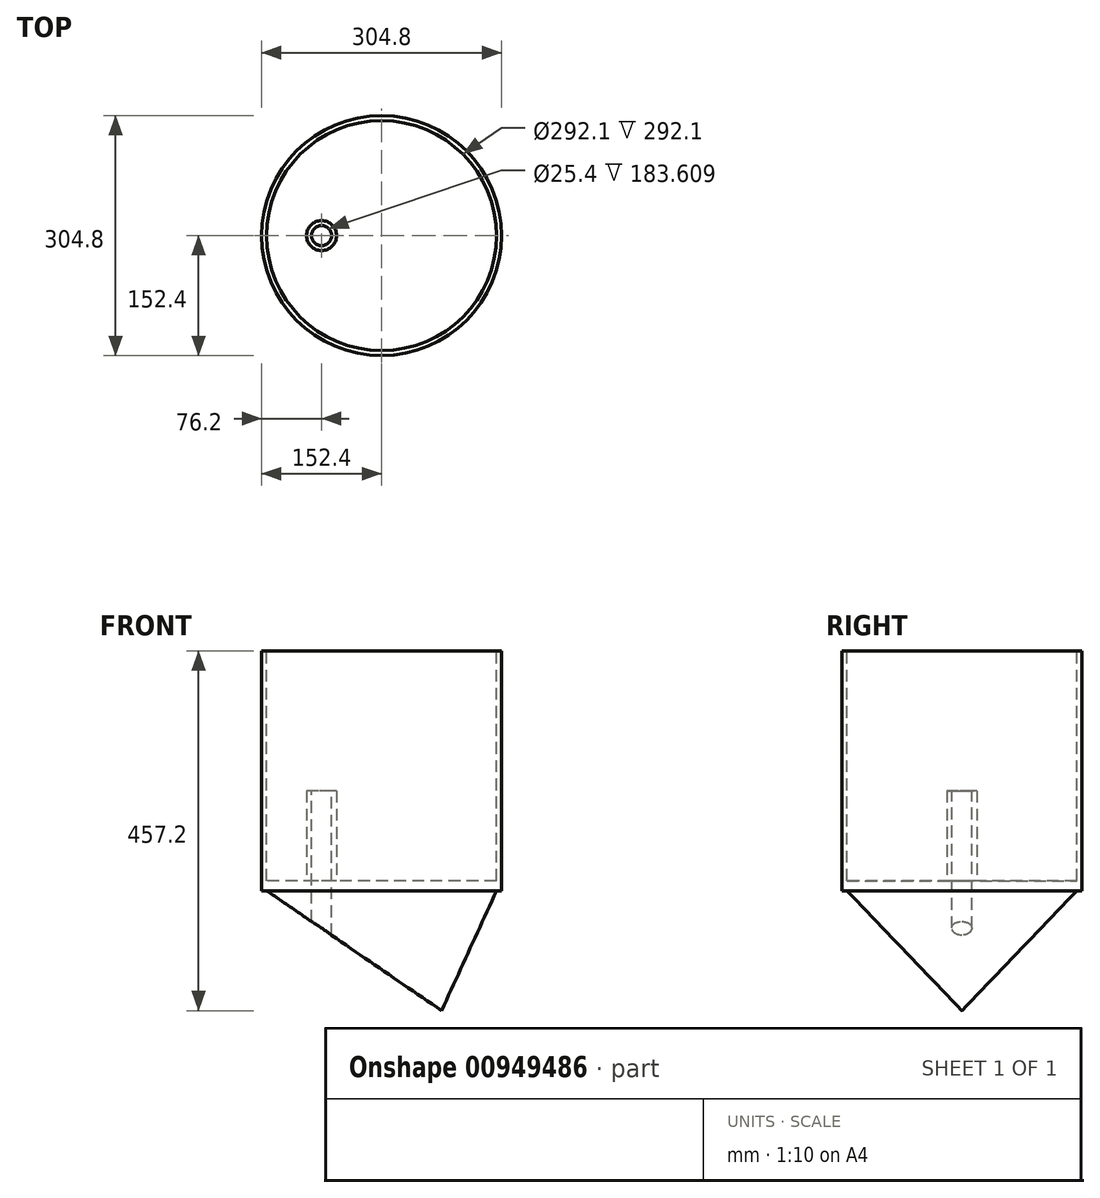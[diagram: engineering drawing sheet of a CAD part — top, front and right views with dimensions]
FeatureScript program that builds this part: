
annotation { "Feature Type Name" : "Feature", "Feature Type Description" : "" }
export const myFeature = defineFeature(function(context is Context, id is Id, definition is map)
    precondition{}
    {
        {
            var Q0;
            Q0=qCreatedBy(makeId("Top.planeOp"),FACE);
            var sketch = newSketch(context, id + "F0", { "sketchPlane" : qUnion([Q0])});
            skCircle(sketch, "E0", {"center": v(0, 0) * mm, "radius": 152.4 * mm});
            skSolve(sketch);
        }
        {
            var Q0;
            Q0=makeQuery(id+"F0.imprint","IMPRINT",FACE,{"disambiguationData":[TD([[makeQuery(id+"F0.imprint","IMPRINT",EDGE,{"derivedFrom":sQuery(id+"F0.wireOp",EDGE,"E0")}),1.0]])]});
            extrude(context, id + "F1", {"entities" : qUnion([Q0]), "depth" : 304.8 * mm, "offsetDistance" : 25.4 * mm});
        }
        {
            var Q0;
            Q0=makeQuery(id+"F1.opExtrude","CAP_FACE",FACE,{"disambiguationData":[OSD([sQuery(id+"F0.wireOp",EDGE,"E0")])],"isStart":false});
            var sketch = newSketch(context, id + "F2", { "sketchPlane" : qUnion([Q0])});
            skCircle(sketch, "E1", {"center": v(0, 0) * mm, "radius": 146.05 * mm});
            skSolve(sketch);
        }
        {
            var Q0;
            Q0=makeQuery(id+"F2.imprint","IMPRINT",FACE,{"disambiguationData":[TD([[makeQuery(id+"F2.imprint","IMPRINT",EDGE,{"derivedFrom":sQuery(id+"F2.wireOp",EDGE,"E1")}),1.0]])]});
            extrude(context, id + "F3", {"entities" : qUnion([Q0]), "operationType" : NewBodyOperationType.REMOVE, "oppositeDirection" : true, "depth" : 292.1 * mm, "offsetDistance" : 25.4 * mm});
        }
        {
            var Q0;
            Q0=makeQuery(id+"F1.opExtrude","CAP_FACE",FACE,{"disambiguationData":[OSD([sQuery(id+"F0.wireOp",EDGE,"E0")])],"isStart":true});
            var sketch = newSketch(context, id + "F4", { "sketchPlane" : qUnion([Q0])});
            skCircle(sketch, "E2", {"center": v(76.2, 0) * mm, "radius": 0.01 * mm});
            skSolve(sketch);
        }
        {
            var Q0;
            Q0=makeQuery(id+"F4.imprint","IMPRINT",FACE,{"disambiguationData":[TD([[makeQuery(id+"F4.imprint","IMPRINT",EDGE,{"derivedFrom":sQuery(id+"F4.wireOp",EDGE,"E2")}),1.0]])]});
            extrude(context, id + "F5", {"entities" : qUnion([Q0]), "operationType" : NewBodyOperationType.ADD, "depth" : 177.8 * mm, "offsetDistance" : 25.4 * mm});
        }
        {
            var Q0;
            Q0=makeQuery(id+"F1.opExtrude","CAP_FACE",FACE,{"disambiguationData":[OSD([sQuery(id+"F0.wireOp",EDGE,"E0")])],"isStart":true});
            var sketch = newSketch(context, id + "F6", { "sketchPlane" : qUnion([Q0])});
            skCircle(sketch, "E3", {"center": v(76.2, 0) * mm, "radius": 0.01 * mm});
            skSolve(sketch);
        }
        {
            var Q0;
            Q0 = qSketchRegion(id + "F6", true);
            extrude(context, id + "F7", {"entities" : qUnion([Q0]), "operationType" : NewBodyOperationType.REMOVE, "depth" : 152.4 * mm, "offsetDistance" : 25.4 * mm});
        }
        {
            var Q0;
            Q0=makeQuery(id+"F7.boolean.opBoolean","MERGE",FACE,{"derivedFrom":[makeQuery(id+"F1.opExtrude","CAP_FACE",FACE,{"disambiguationData":[OSD([sQuery(id+"F0.wireOp",EDGE,"E0")])],"isStart":true})],"fromTools":[makeQuery(id+"F7.opExtrude","CAP_FACE",FACE,{"disambiguationData":[OSD([sQuery(id+"F6.wireOp",EDGE,"E3")])],"isStart":true})]});
            var sketch = newSketch(context, id + "F8", { "sketchPlane" : qUnion([Q0])});
            skCircle(sketch, "E4", {"center": v(0, 0) * mm, "radius": 146.05 * mm});
            skSolve(sketch);
        }
        {
            var Q1;
            Q1 = qSketchRegion(id + "F8", true);
            var Q2;
            Q2=makeQuery(id+"F7.boolean.opBoolean","COPY",FACE,{"derivedFrom":makeQuery(id+"F7.opExtrude","CAP_FACE",FACE,{"disambiguationData":[OSD([sQuery(id+"F6.wireOp",EDGE,"E3")])],"isStart":false})});
            loft(context, id + "F9", {"operationType" : NewBodyOperationType.ADD, "sheetProfilesArray" : [{ "sheetProfileEntities" : qUnion([Q1]) }, { "sheetProfileEntities" : qUnion([Q2]) }]});
        }
        {
            var Q0;
            Q0=makeQuery(id+"F5.opExtrude","CAP_FACE",FACE,{"disambiguationData":[OSD([sQuery(id+"F4.wireOp",EDGE,"E2")])],"isStart":false});
            var sketch = newSketch(context, id + "F10", { "sketchPlane" : qUnion([Q0])});
            skCircle(sketch, "E5", {"center": v(76.2, 0) * mm, "radius": 0.01 * mm});
            skSolve(sketch);
        }
        {
            var Q0;
            Q0 = qSketchRegion(id + "F10", true);
            extrude(context, id + "F11", {"entities" : qUnion([Q0]), "operationType" : NewBodyOperationType.REMOVE, "oppositeDirection" : true, "depth" : 25.4 * mm, "offsetDistance" : 25.4 * mm});
        }
        {
            var Q0;
            Q0=makeQuery(id+"F3.boolean.opBoolean","COPY",FACE,{"derivedFrom":makeQuery(id+"F3.opExtrude","CAP_FACE",FACE,{"disambiguationData":[OSD([sQuery(id+"F2.wireOp",EDGE,"E1")])],"isStart":false})});
            var sketch = newSketch(context, id + "F12", { "sketchPlane" : qUnion([Q0])});
            skCircle(sketch, "E6", {"center": v(-76.2, 0) * mm, "radius": 12.7 * mm});
            skSolve(sketch);
        }
        {
            var Q0;
            Q0=makeQuery(id+"F12.imprint","IMPRINT",FACE,{"disambiguationData":[TD([[makeQuery(id+"F12.imprint","IMPRINT",EDGE,{"derivedFrom":sQuery(id+"F12.wireOp",EDGE,"E6")}),1.0]])]});
            extrude(context, id + "F13", {"entities" : qUnion([Q0]), "operationType" : NewBodyOperationType.REMOVE, "oppositeDirection" : true, "depth" : 165.1 * mm, "offsetDistance" : 25.4 * mm});
        }
        {
            var Q0;
            Q0=makeQuery(id+"F3.boolean.opBoolean","COPY",FACE,{"derivedFrom":makeQuery(id+"F3.opExtrude","CAP_FACE",FACE,{"disambiguationData":[OSD([sQuery(id+"F2.wireOp",EDGE,"E1")])],"isStart":false})});
            var sketch = newSketch(context, id + "F14", { "sketchPlane" : qUnion([Q0])});
            skCircle(sketch, "E7", {"center": v(-76.2, 0) * mm, "radius": 19.05 * mm});
            skCircle(sketch, "E8", {"center": v(-76.2, 0) * mm, "radius": 12.7 * mm});
            skSolve(sketch);
        }
        {
            var Q0;
            Q0=makeQuery(id+"F14.imprint","IMPRINT",FACE,{"disambiguationData":[TD([[makeQuery(id+"F14.imprint","IMPRINT",EDGE,{"derivedFrom":sQuery(id+"F14.wireOp",EDGE,"E7")}),1.0]])]});
            extrude(context, id + "F15", {"entities" : qUnion([Q0]), "operationType" : NewBodyOperationType.ADD, "depth" : 114.3 * mm, "offsetDistance" : 25.4 * mm});
        }
    });
